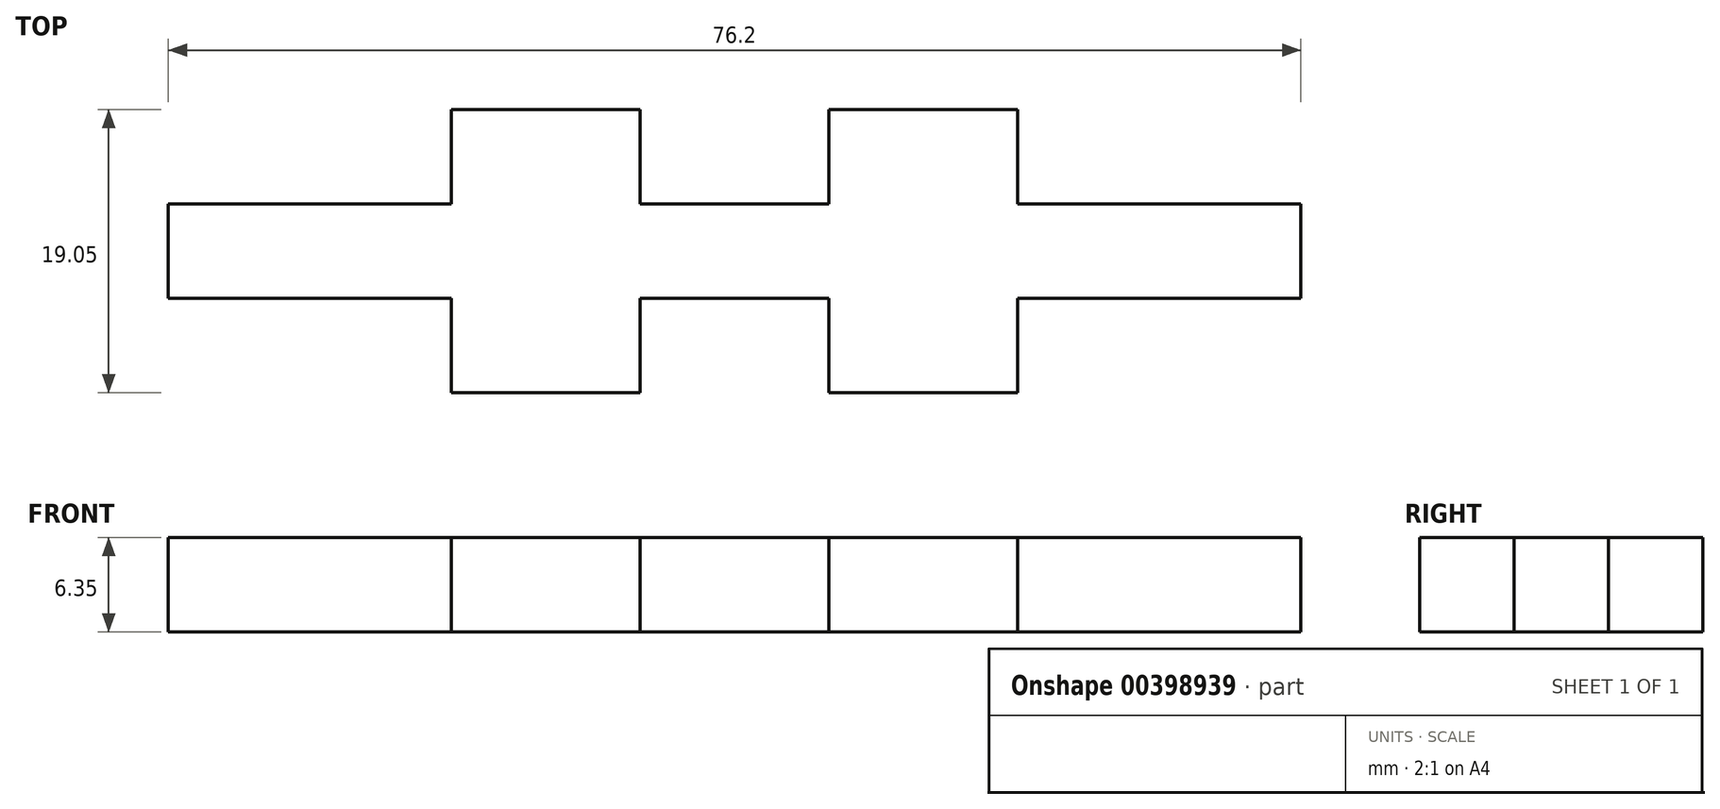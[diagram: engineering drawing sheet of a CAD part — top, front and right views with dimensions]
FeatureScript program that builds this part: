
annotation { "Feature Type Name" : "Feature", "Feature Type Description" : "" }
export const myFeature = defineFeature(function(context is Context, id is Id, definition is map)
    precondition{}
    {
        {
            var Q0;
            Q0=qCreatedBy(makeId("Top.planeOp"),FACE);
            var sketch = newSketch(context, id + "F0", { "sketchPlane" : qUnion([Q0])});
            skLineSegment(sketch, "E0.bottom", {"start": v(19.05, 0) * mm, "end": v(31.75, 0) * mm});
            skLineSegment(sketch, "E0.top", {"start": v(19.05, -19.05) * mm, "end": v(31.75, -19.05) * mm});
            skLineSegment(sketch, "E0.left", {"start": v(0, -6.35) * mm, "end": v(0, -12.7) * mm});
            skLineSegment(sketch, "E0.right", {"start": v(76.2, -6.35) * mm, "end": v(76.2, -12.7) * mm});
            skLineSegment(sketch, "E1", {"start": v(0, -6.35) * mm, "end": v(19.05, -6.35) * mm});
            skLineSegment(sketch, "E2", {"start": v(19.05, -6.35) * mm, "end": v(19.05, 0) * mm});
            skLineSegment(sketch, "E3", {"start": v(31.75, 0) * mm, "end": v(31.75, -6.35) * mm});
            skLineSegment(sketch, "E4", {"start": v(31.75, -6.35) * mm, "end": v(44.45, -6.35) * mm});
            skLineSegment(sketch, "E5", {"start": v(44.45, -6.35) * mm, "end": v(44.45, 0) * mm});
            skLineSegment(sketch, "E6", {"start": v(44.45, 0) * mm, "end": v(57.15, 0) * mm});
            skLineSegment(sketch, "E7", {"start": v(57.15, 0) * mm, "end": v(57.15, -6.35) * mm});
            skLineSegment(sketch, "E8", {"start": v(57.15, -6.35) * mm, "end": v(76.2, -6.35) * mm});
            skPoint(sketch, "E9.orphan", {"position": v(0, 0) * mm});
            skPoint(sketch, "E10.orphan", {"position": v(76.2, 0) * mm});
            skLineSegment(sketch, "E11", {"start": v(0, -12.7) * mm, "end": v(19.05, -12.7) * mm});
            skLineSegment(sketch, "E12", {"start": v(19.05, -12.7) * mm, "end": v(19.05, -19.05) * mm});
            skLineSegment(sketch, "E13", {"start": v(31.75, -19.05) * mm, "end": v(31.75, -12.7) * mm});
            skLineSegment(sketch, "E14", {"start": v(31.75, -12.7) * mm, "end": v(44.45, -12.7) * mm});
            skLineSegment(sketch, "E15", {"start": v(44.45, -12.7) * mm, "end": v(44.45, -19.05) * mm});
            skLineSegment(sketch, "E16", {"start": v(44.45, -19.05) * mm, "end": v(57.15, -19.05) * mm});
            skLineSegment(sketch, "E17", {"start": v(57.15, -19.05) * mm, "end": v(57.15, -12.7) * mm});
            skLineSegment(sketch, "E18", {"start": v(57.15, -12.7) * mm, "end": v(76.2, -12.7) * mm});
            skPoint(sketch, "E19.start.orphan", {"position": v(0, -19.05) * mm});
            skSolve(sketch);
        }
        {
            var Q0;
            Q0=makeQuery(id+"F0.imprint","IMPRINT",FACE,{"disambiguationData":[TD([[makeQuery(id+"F0.imprint","IMPRINT",EDGE,{"derivedFrom":sQuery(id+"F0.wireOp",EDGE,"E0.left")}),1.0]])]});
            extrude(context, id + "F1", {"entities" : qUnion([Q0]), "depth" : 6.35 * mm, "offsetDistance" : 25.4 * mm});
        }
    });
